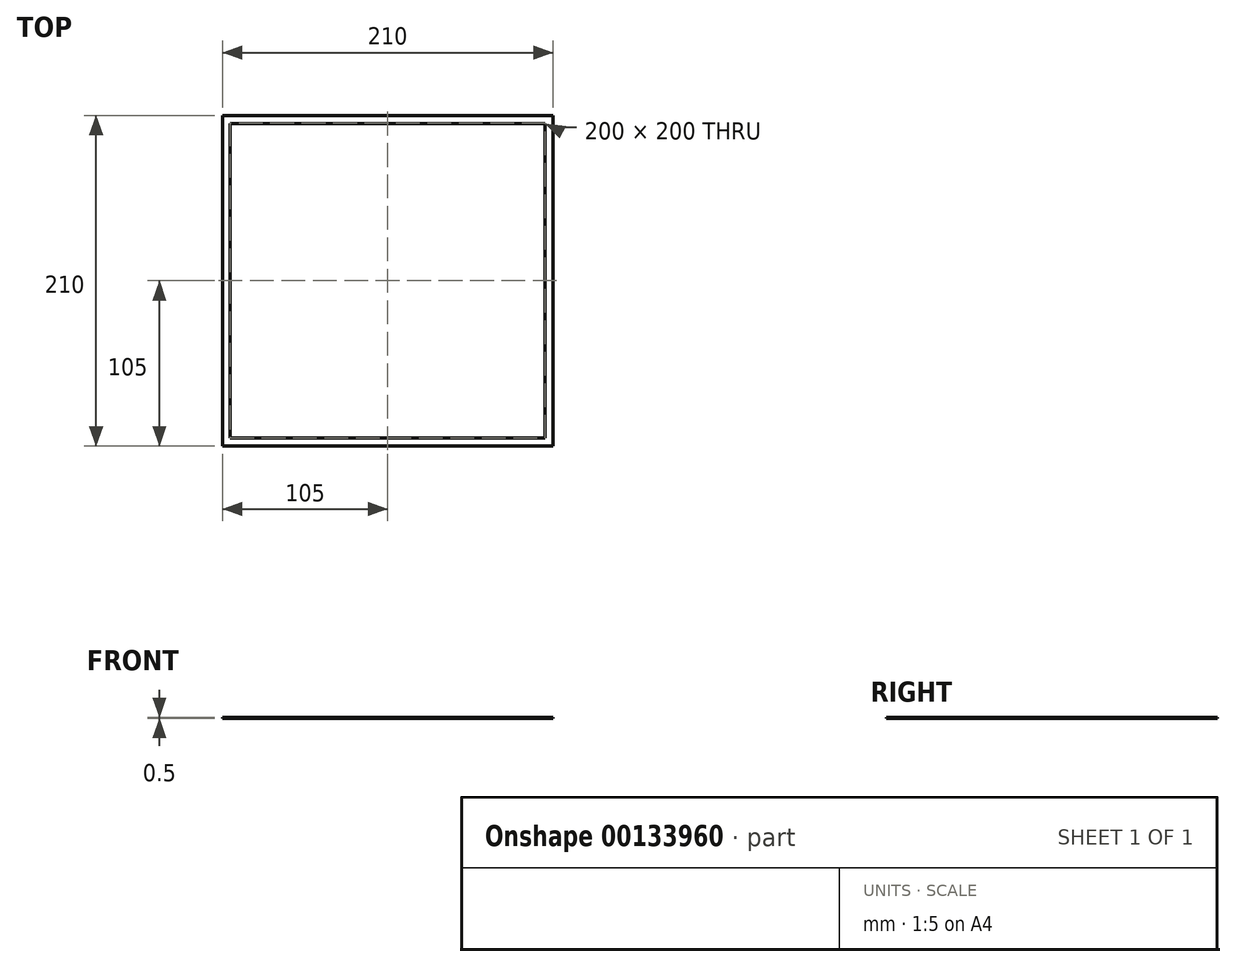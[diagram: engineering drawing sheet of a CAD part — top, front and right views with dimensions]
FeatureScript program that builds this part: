
annotation { "Feature Type Name" : "Feature", "Feature Type Description" : "" }
export const myFeature = defineFeature(function(context is Context, id is Id, definition is map)
    precondition{}
    {
        {
            var Q0;
            Q0=qCreatedBy(makeId("Top.planeOp"),FACE);
            var sketch = newSketch(context, id + "F0", { "sketchPlane" : qUnion([Q0])});
            skLineSegment(sketch, "E0.bottom", {"start": v(100, -100) * mm, "end": v(-100, -100) * mm});
            skLineSegment(sketch, "E0.top", {"start": v(100, 100) * mm, "end": v(-100, 100) * mm});
            skLineSegment(sketch, "E0.left", {"start": v(100, -100) * mm, "end": v(100, 100) * mm});
            skLineSegment(sketch, "E0.right", {"start": v(-100, -100) * mm, "end": v(-100, 100) * mm});
            skPoint(sketch, "E0.middle", {"position": v(0, 0) * mm});
            skLineSegment(sketch, "E1.0", {"start": v(105, 105) * mm, "end": v(-105, 105) * mm});
            skLineSegment(sketch, "E1.1", {"start": v(105, -105) * mm, "end": v(105, 105) * mm});
            skLineSegment(sketch, "E1.2", {"start": v(105, -105) * mm, "end": v(-105, -105) * mm});
            skLineSegment(sketch, "E1.3", {"start": v(-105, -105) * mm, "end": v(-105, 105) * mm});
            skSolve(sketch);
        }
        {
            var Q0;
            Q0 = qSketchRegion(id + "F0", true);
            extrude(context, id + "F1", {"entities" : qUnion([Q0]), "depth" : 0.5 * mm});
        }
    });
